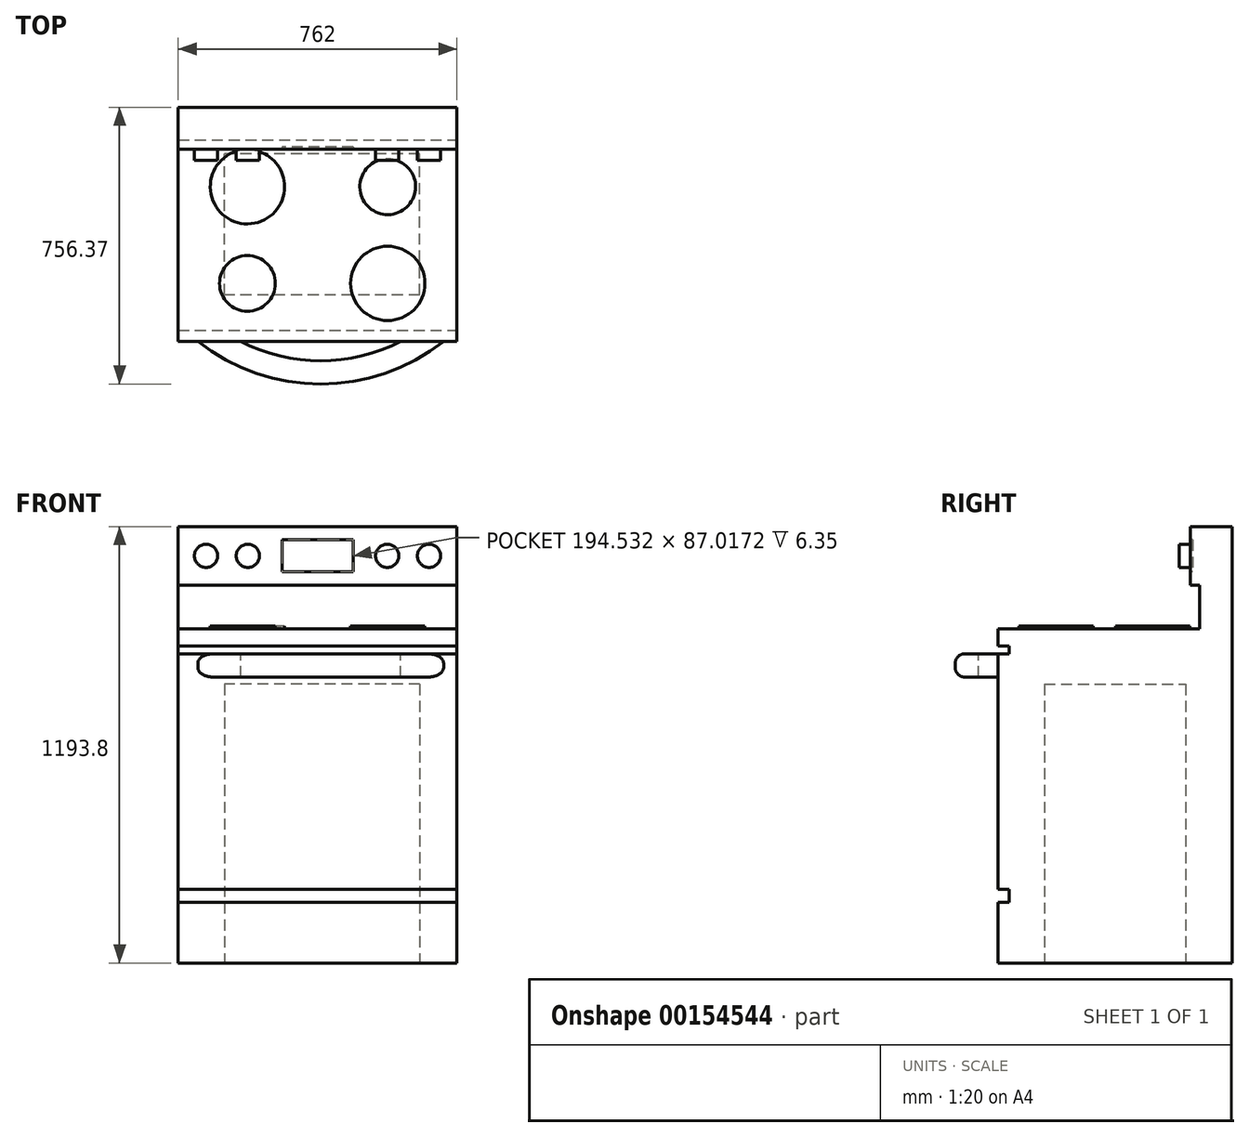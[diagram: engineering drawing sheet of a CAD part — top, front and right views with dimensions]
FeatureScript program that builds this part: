
annotation { "Feature Type Name" : "Feature", "Feature Type Description" : "" }
export const myFeature = defineFeature(function(context is Context, id is Id, definition is map)
    precondition{}
    {
        {
            var Q0;
            Q0=qCreatedBy(makeId("Top.planeOp"),FACE);
            var sketch = newSketch(context, id + "F0", { "sketchPlane" : qUnion([Q0])});
            skLineSegment(sketch, "E0.bottom", {"start": v(381, 304.8) * mm, "end": v(-381, 304.8) * mm});
            skLineSegment(sketch, "E0.top", {"start": v(381, -304.8) * mm, "end": v(-381, -304.8) * mm});
            skLineSegment(sketch, "E0.left", {"start": v(381, 304.8) * mm, "end": v(381, -304.8) * mm});
            skLineSegment(sketch, "E0.right", {"start": v(-381, 304.8) * mm, "end": v(-381, -304.8) * mm});
            skPoint(sketch, "E0.middle", {"position": v(0, 0) * mm});
            skSolve(sketch);
        }
        {
            var Q0;
            Q0=makeQuery(id+"F0.imprint","IMPRINT",FACE,{"disambiguationData":[TD([[makeQuery(id+"F0.imprint","IMPRINT",EDGE,{"derivedFrom":sQuery(id+"F0.wireOp",EDGE,"E0.bottom")}),1.0]])]});
            extrude(context, id + "F1", {"entities" : qUnion([Q0]), "depth" : 914.4 * mm});
        }
        {
            var Q0;
            Q0=makeQuery(id+"F1.opExtrude","CAP_FACE",FACE,{"disambiguationData":[OSD([sQuery(id+"F0.wireOp",EDGE,"E0.bottom"),sQuery(id+"F0.wireOp",EDGE,"E0.top"),sQuery(id+"F0.wireOp",EDGE,"E0.left"),sQuery(id+"F0.wireOp",EDGE,"E0.right")])],"isStart":false});
            var sketch = newSketch(context, id + "F2", { "sketchPlane" : qUnion([Q0])});
            skLineSegment(sketch, "E1.bottom", {"start": v(-381, 304.8) * mm, "end": v(381, 304.8) * mm});
            skLineSegment(sketch, "E1.top", {"start": v(-381, 215.9) * mm, "end": v(381, 215.9) * mm});
            skLineSegment(sketch, "E1.left", {"start": v(-381, 304.8) * mm, "end": v(-381, 215.9) * mm});
            skLineSegment(sketch, "E1.right", {"start": v(381, 304.8) * mm, "end": v(381, 215.9) * mm});
            skCircle(sketch, "E2", {"center": v(-191.76, 87.73) * mm, "radius": 101.6 * mm});
            skCircle(sketch, "E3", {"center": v(-191.76, -176.63) * mm, "radius": 76.2 * mm});
            skCircle(sketch, "E4", {"center": v(191.76, 87.73) * mm, "radius": 76.2 * mm});
            skCircle(sketch, "E5", {"center": v(191.76, -176.63) * mm, "radius": 101.6 * mm});
            skLineSegment(sketch, "E6", {"start": v(-191.76, 87.73) * mm, "end": v(-191.76, -176.63) * mm, "construction": true});
            skLineSegment(sketch, "E7", {"start": v(191.76, -176.63) * mm, "end": v(-191.76, -176.63) * mm, "construction": true});
            skLineSegment(sketch, "E8", {"start": v(-191.76, 87.73) * mm, "end": v(191.76, 87.73) * mm, "construction": true});
            skLineSegment(sketch, "E9", {"start": v(191.76, -176.63) * mm, "end": v(191.76, 87.73) * mm, "construction": true});
            skLineSegment(sketch, "E10", {"start": v(0, 215.9) * mm, "end": v(0, 87.73) * mm, "construction": true});
            skLineSegment(sketch, "E11", {"start": v(0, 87.73) * mm, "end": v(0, -176.63) * mm, "construction": true});
            skLineSegment(sketch, "E12", {"start": v(0, -176.63) * mm, "end": v(0, -304.8) * mm, "construction": true});
            skPoint(sketch, "E12.endSnap0", {"position": v(0, -304.8) * mm});
            skLineSegment(sketch, "E13", {"start": v(381, -44.45) * mm, "end": v(191.76, -44.45) * mm, "construction": true});
            skLineSegment(sketch, "E14", {"start": v(191.76, -44.45) * mm, "end": v(-191.76, -44.45) * mm, "construction": true});
            skLineSegment(sketch, "E15", {"start": v(-191.76, -44.45) * mm, "end": v(-381, -44.45) * mm, "construction": true});
            skPoint(sketch, "E15.endSnap0", {"position": v(-381, 0) * mm});
            skLineSegment(sketch, "E16", {"start": v(-381, 215.9) * mm, "end": v(-381, -304.8) * mm, "construction": true});
            skSolve(sketch);
        }
        {
            var Q0;
            Q0=makeQuery(id+"F2.imprint","IMPRINT",FACE,{"disambiguationData":[TD([[makeQuery(id+"F2.imprint","IMPRINT",EDGE,{"derivedFrom":sQuery(id+"F2.wireOp",EDGE,"E2")}),1.0]])]});
            var Q1;
            Q1=makeQuery(id+"F2.imprint","IMPRINT",FACE,{"disambiguationData":[TD([[makeQuery(id+"F2.imprint","IMPRINT",EDGE,{"derivedFrom":sQuery(id+"F2.wireOp",EDGE,"E3")}),1.0]])]});
            var Q2;
            Q2=makeQuery(id+"F2.imprint","IMPRINT",FACE,{"disambiguationData":[TD([[makeQuery(id+"F2.imprint","IMPRINT",EDGE,{"derivedFrom":sQuery(id+"F2.wireOp",EDGE,"E4")}),1.0]])]});
            var Q3;
            Q3=makeQuery(id+"F2.imprint","IMPRINT",FACE,{"disambiguationData":[TD([[makeQuery(id+"F2.imprint","IMPRINT",EDGE,{"derivedFrom":sQuery(id+"F2.wireOp",EDGE,"E5")}),1.0]])]});
            extrude(context, id + "F3", {"entities" : qUnion([Q0, Q1, Q2, Q3]), "operationType" : NewBodyOperationType.ADD, "depth" : 7.62 * mm});
        }
        {
            var Q0;
            Q0=makeQuery(id+"F2.imprint","IMPRINT",FACE,{"disambiguationData":[TD([[makeQuery(id+"F2.imprint","IMPRINT",EDGE,{"derivedFrom":sQuery(id+"F2.wireOp",EDGE,"E1.bottom")}),1.0]])]});
            extrude(context, id + "F4", {"entities" : qUnion([Q0]), "operationType" : NewBodyOperationType.ADD, "depth" : 279.4 * mm});
        }
        {
            var Q0;
            Q0=makeQuery(id+"F1.opExtrude","SWEPT_FACE",FACE,{"disambiguationData":[OSD([sQuery(id+"F0.wireOp",EDGE,"E0.top")])]});
            var sketch = newSketch(context, id + "F5", { "sketchPlane" : qUnion([Q0])});
            skLineSegment(sketch, "E17.bottom", {"start": v(-381, 845.54) * mm, "end": v(381, 845.54) * mm});
            skLineSegment(sketch, "E17.top", {"start": v(-381, 201.57) * mm, "end": v(381, 201.57) * mm});
            skLineSegment(sketch, "E17.left", {"start": v(-381, 845.54) * mm, "end": v(-381, 201.57) * mm});
            skLineSegment(sketch, "E17.right", {"start": v(381, 845.54) * mm, "end": v(381, 201.57) * mm});
            skLineSegment(sketch, "E18.bottom", {"start": v(-381, 166.34) * mm, "end": v(381, 166.34) * mm});
            skLineSegment(sketch, "E18.top", {"start": v(-381, 0) * mm, "end": v(381, 0) * mm});
            skLineSegment(sketch, "E18.left", {"start": v(-381, 166.34) * mm, "end": v(-381, 0) * mm});
            skLineSegment(sketch, "E18.right", {"start": v(381, 166.34) * mm, "end": v(381, 0) * mm});
            skLineSegment(sketch, "E19.bottom", {"start": v(-381, 914.4) * mm, "end": v(381, 914.4) * mm});
            skLineSegment(sketch, "E19.top", {"start": v(-381, 867.3) * mm, "end": v(381, 867.3) * mm});
            skLineSegment(sketch, "E19.left", {"start": v(-381, 914.4) * mm, "end": v(-381, 867.3) * mm});
            skLineSegment(sketch, "E19.right", {"start": v(381, 914.4) * mm, "end": v(381, 867.3) * mm});
            skSolve(sketch);
        }
        {
            var Q0;
            Q0=makeQuery(id+"F5.imprint","IMPRINT",FACE,{"disambiguationData":[TD([[makeQuery(id+"F5.imprint","IMPRINT",EDGE,{"derivedFrom":sQuery(id+"F5.wireOp",EDGE,"E19.bottom")}),1.0]])]});
            var Q1;
            Q1=makeQuery(id+"F5.imprint","IMPRINT",FACE,{"disambiguationData":[TD([[makeQuery(id+"F5.imprint","IMPRINT",EDGE,{"derivedFrom":sQuery(id+"F5.wireOp",EDGE,"E17.bottom")}),-1.0]])]});
            var Q2;
            Q2=makeQuery(id+"F5.imprint","IMPRINT",FACE,{"disambiguationData":[TD([[makeQuery(id+"F5.imprint","IMPRINT",EDGE,{"derivedFrom":sQuery(id+"F5.wireOp",EDGE,"E18.bottom")}),-1.0]])]});
            extrude(context, id + "F6", {"entities" : qUnion([Q0, Q1, Q2]), "operationType" : NewBodyOperationType.ADD, "depth" : 30.48 * mm});
        }
        {
            var Q0;
            Q0=makeQuery(id+"F6.opExtrude","SWEPT_FACE",FACE,{"disambiguationData":[OSD([sQuery(id+"F5.wireOp",EDGE,"E17.bottom")])]});
            var sketch = newSketch(context, id + "F7", { "sketchPlane" : qUnion([Q0])});
            skCircle(sketch, "E20", {"center": v(8.6, 91.69) * mm, "radius": 543.26 * mm});
            skPoint(sketch, "E20.first.point", {"position": v(-327.3, -335.28) * mm});
            skPoint(sketch, "E20.second.point", {"position": v(344.5, -335.28) * mm});
            skPoint(sketch, "E20.third.point", {"position": v(0, -451.5) * mm});
            skLineSegment(sketch, "E21", {"start": v(-327.3, -335.28) * mm, "end": v(344.5, -335.28) * mm});
            skCircle(sketch, "E22.0", {"center": v(8.6, 91.69) * mm, "radius": 479.76 * mm});
            skSolve(sketch);
        }
        {
            var Q0;
            {var subQ0=sQuery(id+"F7.wireOp",EDGE,"E21");var subQ5=sQuery(id+"F7.wireOp",EDGE,"E22.0");var subQ6=makeQuery(id+"F7.imprint","INTERSECT",VERTEX,{"disambiguationData":[OD(0.0)],"derivedFrom":[subQ0,subQ5]});Q0=makeQuery(id+"F7.imprint","IMPRINT",FACE,{"disambiguationData":[TD([[makeQuery(id+"F7.imprint","IMPRINT",EDGE,{"disambiguationData":[TD([[subQ6,-1.0]])],"derivedFrom":subQ5}),-1.0]])]});}
            extrude(context, id + "F8", {"entities" : qUnion([Q0]), "operationType" : NewBodyOperationType.ADD, "oppositeDirection" : true, "depth" : 63.5 * mm});
        }
        {
            var Q0;
            Q0=makeQuery(id+"F8.opExtrude","CAP_EDGE",EDGE,{"disambiguationData":[OSD([sQuery(id+"F7.wireOp",EDGE,"E20")])],"isStart":true});
            var Q1;
            Q1=makeQuery(id+"F8.opExtrude","CAP_EDGE",EDGE,{"disambiguationData":[OSD([sQuery(id+"F7.wireOp",EDGE,"E20")])],"isStart":false});
            fillet(context, id + "F9", {"entities" : qUnion([Q0, Q1]), "radius" : 25.4 * mm, "tangentPropagation" : true, "allowEdgeOverflow" : false});
        }
        {
            var Q0;
            Q0=makeQuery(id+"F4.opExtrude","SWEPT_FACE",FACE,{"disambiguationData":[OSD([sQuery(id+"F2.wireOp",EDGE,"E1.top")])]});
            var sketch = newSketch(context, id + "F10", { "sketchPlane" : qUnion([Q0])});
            skLineSegment(sketch, "E23.bottom", {"start": v(-381, 1193.8) * mm, "end": v(381, 1193.8) * mm});
            skLineSegment(sketch, "E23.top", {"start": v(-381, 1033.53) * mm, "end": v(381, 1033.53) * mm});
            skLineSegment(sketch, "E23.left", {"start": v(-381, 1193.8) * mm, "end": v(-381, 1033.53) * mm});
            skLineSegment(sketch, "E23.right", {"start": v(381, 1193.8) * mm, "end": v(381, 1033.53) * mm});
            skSolve(sketch);
        }
        {
            var Q0;
            Q0=makeQuery(id+"F10.imprint","IMPRINT",FACE,{"disambiguationData":[TD([[makeQuery(id+"F10.imprint","IMPRINT",EDGE,{"derivedFrom":sQuery(id+"F10.wireOp",EDGE,"E23.bottom")}),-1.0]])]});
            extrude(context, id + "F11", {"entities" : qUnion([Q0]), "operationType" : NewBodyOperationType.ADD, "depth" : 25.4 * mm});
        }
        {
            var Q0;
            Q0=makeQuery(id+"F11.opExtrude","CAP_FACE",FACE,{"disambiguationData":[OSD([sQuery(id+"F10.wireOp",EDGE,"E23.bottom"),sQuery(id+"F10.wireOp",EDGE,"E23.top"),sQuery(id+"F10.wireOp",EDGE,"E23.left"),sQuery(id+"F10.wireOp",EDGE,"E23.right")])],"isStart":false});
            var sketch = newSketch(context, id + "F12", { "sketchPlane" : qUnion([Q0])});
            skLineSegment(sketch, "E24", {"start": v(-381, 1113.66) * mm, "end": v(381, 1113.66) * mm, "construction": true});
            skCircle(sketch, "E25", {"center": v(-304.8, 1113.66) * mm, "radius": 31.75 * mm});
            skCircle(sketch, "E26", {"center": v(-190.5, 1113.66) * mm, "radius": 31.75 * mm});
            skCircle(sketch, "E27", {"center": v(190.5, 1113.66) * mm, "radius": 31.75 * mm});
            skCircle(sketch, "E28", {"center": v(304.8, 1113.66) * mm, "radius": 31.75 * mm});
            skLineSegment(sketch, "E29.bottom", {"start": v(97.27, 1157.17) * mm, "end": v(-97.27, 1157.17) * mm});
            skLineSegment(sketch, "E29.top", {"start": v(97.27, 1070.15) * mm, "end": v(-97.27, 1070.15) * mm});
            skLineSegment(sketch, "E29.left", {"start": v(97.27, 1157.17) * mm, "end": v(97.27, 1070.15) * mm});
            skLineSegment(sketch, "E29.right", {"start": v(-97.27, 1157.17) * mm, "end": v(-97.27, 1070.15) * mm});
            skPoint(sketch, "E29.middle", {"position": v(0, 1113.66) * mm});
            skSolve(sketch);
        }
        {
            var Q0;
            Q0=makeQuery(id+"F12.imprint","IMPRINT",FACE,{"disambiguationData":[TD([[makeQuery(id+"F12.imprint","IMPRINT",EDGE,{"derivedFrom":sQuery(id+"F12.wireOp",EDGE,"E25")}),1.0]])]});
            var Q1;
            Q1=makeQuery(id+"F12.imprint","IMPRINT",FACE,{"disambiguationData":[TD([[makeQuery(id+"F12.imprint","IMPRINT",EDGE,{"derivedFrom":sQuery(id+"F12.wireOp",EDGE,"E26")}),1.0]])]});
            var Q2;
            Q2=makeQuery(id+"F12.imprint","IMPRINT",FACE,{"disambiguationData":[TD([[makeQuery(id+"F12.imprint","IMPRINT",EDGE,{"derivedFrom":sQuery(id+"F12.wireOp",EDGE,"E27")}),1.0]])]});
            var Q3;
            Q3=makeQuery(id+"F12.imprint","IMPRINT",FACE,{"disambiguationData":[TD([[makeQuery(id+"F12.imprint","IMPRINT",EDGE,{"derivedFrom":sQuery(id+"F12.wireOp",EDGE,"E28")}),1.0]])]});
            extrude(context, id + "F13", {"entities" : qUnion([Q0, Q1, Q2, Q3]), "operationType" : NewBodyOperationType.ADD, "depth" : 30.48 * mm});
        }
        {
            var Q0;
            Q0=makeQuery(id+"F12.imprint","IMPRINT",FACE,{"disambiguationData":[TD([[makeQuery(id+"F12.imprint","IMPRINT",EDGE,{"derivedFrom":sQuery(id+"F12.wireOp",EDGE,"E29.bottom")}),1.0]])]});
            extrude(context, id + "F14", {"entities" : qUnion([Q0]), "operationType" : NewBodyOperationType.REMOVE, "oppositeDirection" : true, "depth" : 6.35 * mm});
        }
        {
            var Q0;
            Q0=makeQuery(id+"F6.boolean.opBoolean","MERGE",FACE,{"derivedFrom":[makeQuery(id+"F1.opExtrude","CAP_FACE",FACE,{"disambiguationData":[OSD([sQuery(id+"F0.wireOp",EDGE,"E0.bottom"),sQuery(id+"F0.wireOp",EDGE,"E0.top"),sQuery(id+"F0.wireOp",EDGE,"E0.left"),sQuery(id+"F0.wireOp",EDGE,"E0.right")])],"isStart":true}),makeQuery(id+"F6.opExtrude","SWEPT_FACE",FACE,{"disambiguationData":[OSD([sQuery(id+"F5.wireOp",EDGE,"E18.top")])]})]});
            var sketch = newSketch(context, id + "F15", { "sketchPlane" : qUnion([Q0])});
            skLineSegment(sketch, "E30.bottom", {"start": v(279.4, 208.28) * mm, "end": v(-254, 208.28) * mm});
            skLineSegment(sketch, "E30.top", {"start": v(279.4, -177.8) * mm, "end": v(-254, -177.8) * mm});
            skLineSegment(sketch, "E30.left", {"start": v(279.4, 208.28) * mm, "end": v(279.4, -177.8) * mm});
            skLineSegment(sketch, "E30.right", {"start": v(-254, 208.28) * mm, "end": v(-254, -177.8) * mm});
            skSolve(sketch);
        }
        {
            var Q0;
            Q0=makeQuery(id+"F15.imprint","IMPRINT",FACE,{"disambiguationData":[TD([[makeQuery(id+"F15.imprint","IMPRINT",EDGE,{"derivedFrom":sQuery(id+"F15.wireOp",EDGE,"E30.bottom")}),1.0]])]});
            extrude(context, id + "F16", {"entities" : qUnion([Q0]), "operationType" : NewBodyOperationType.REMOVE, "oppositeDirection" : true, "depth" : 762.76 * mm});
        }
    });
